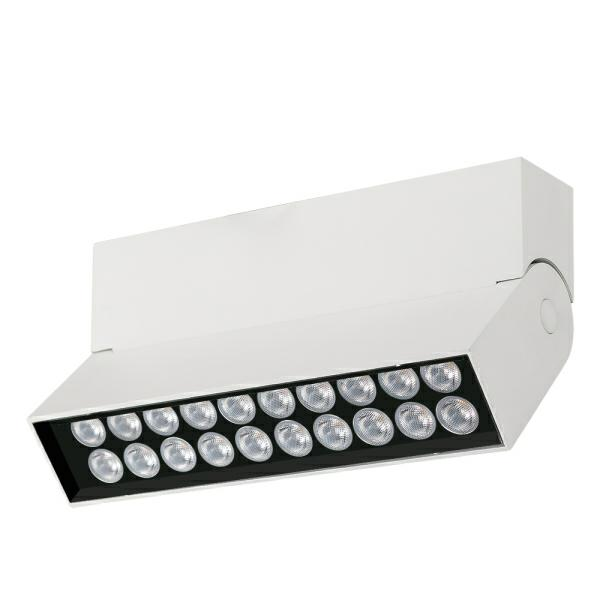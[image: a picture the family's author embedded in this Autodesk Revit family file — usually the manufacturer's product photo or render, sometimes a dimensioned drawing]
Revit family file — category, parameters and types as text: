
# Revit family: LOFT-SURFACE-10W
name_source: partatom
category: Осветительные приборы
revit_build: Autodesk Revit 2017 (Build: 20160225_1515(x64)
units: mm (PartAtom-declared; Revit-internal decimal feet)

## family parameters
Всегда вертикально = Да
Источник света = Да
На основе рабочей плоскости = Нет
Общий = Нет
При загрузке вырезать с полостями = Нет
Размер круглого соединителя = Использовать диаметр
Тип детали = Нормальный
Точка расчета площади = Нет

## types (6) — shared parameters
ADSK_Единица измерения = шт.
ADSK_Завод-изготовитель = ARLIGHT
ADSK_Классификация нагрузок = Освещение
ADSK_Количество фаз = 1
ADSK_Количество фаз числовое = 1
ADSK_Коэффициент мощности = 0.95
ADSK_Масса_Текст = 0.565
ADSK_Наименование = Светильник
ADSK_Напряжение = 230 В
ADSK_Номинальная мощность = 10 Вт
ADSK_Полная мощность = 11 В·А
ADSK_Размер_Высота = 100 мм
ADSK_Размер_Длина = 170 мм
ADSK_Размер_Ширина = 36 мм
ADSK_Ток = 0 А
ARL_Драйвер = Встроенный (DC300mA 25-40V)
ARL_Индекс цветопередачи = >90
ARL_Класс защиты от поражения электрическим током = I
ARL_Класс пылевлагозащиты = IP40
ARL_Область использования = Для освещения в квартирах, офисах, музеях, магазинах с высокими требованиями к качеству света
ARL_Рабочая температура окружающей среды = -20...+40 °C
ARL_Серия = LOFT
ARL_Способ монтажа = Накладной
ARL_Тип товара = Светильник
ARL_Угол обзора = 24°
URL = https://arlight.ru
Видимая форма излучения при визуализации = Нет
Группа модели = Светильники
Изготовитель = ARLIGHT
Изготовитель (сайт) = www.arlight.ru
Изготовитель (телефон) = 8 800 505 26 29
Излучение по длине прямоугольника = 168 мм
Излучение по ширине прямоугольника = 34 мм
Полная установленная мощность = 11 В·А
Разработчик = НТЦ Конструктор
Разработчик (URL) = https://constructor.ru
Разработчик (телефон) = +7 (495) 781-05-35
Светофильтр = 16777215
Смещение цветовой температуры при затухании лампы = <Нет>
Угол наклона = 90.00°

## per-type parameters (varying)
| type | ADSK_Код изделия | ADSK_Марка | ARL_Материал корпуса | ARL_Обозначение корпуса | ARL_Цвет покрытия | ARL_Цвет свечения | Комментарии к типоразмеру | Описание | Файл фотометрической сетки |
| 026212 Светильник SP-LOFT-SURFACE-S170-10W White6000 (WH, 24 deg) | Арт. 026214 | SP-LOFT-SURFACE-S170-10W Warm3000 | Металл, белый | Корпус прямоугольный, алюминий, цвет белый | Белый | Теплый 3000K | Арт. 026214 | Накладной поворотный светильник 10 Вт. Цвет ТЕПЛЫЙ 3000K, св.поток 500-550лм, CRI(Ra)>90, угол 24°. Угол наклона 45°. Корпус прямоугольный, белый алюминий, IP40. Размер LxHxW 170x100x36 мм. Питание AC 220-240V, 10 Вт, драйвер встроенный (DC300mA 25-40V) | 026214_SP-LOFT-SURFACE-S170-10W Warm3000 (WH, 24 deg).ies |
| 026213 Светильник SP-LOFT-SURFACE-S170-10W Day4000 (WH, 24 deg) | Арт. 026213 | SP-LOFT-SURFACE-S170-10W Day4000 | Металл, белый | Корпус прямоугольный, алюминий, цвет белый | Белый | Дневной 4000K | Арт. 026213 | Накладной поворотный светильник 10 Вт. Цвет ДНЕВНОЙ 4000K, св.поток 540-600лм, CRI(Ra)>90, угол 24°. Угол наклона 45°. Корпус прямоугольный, белый алюминий, IP40. Размер LxHxW 170x100x36 мм. Питание AC 220-240V, 10 Вт, драйвер встроенный (DC300mA 25-40V) | 026213_SP-LOFT-SURFACE-S170-10W Day4000 (WH, 24 deg).ies |
| 026214 Светильник SP-LOFT-SURFACE-S170-10W Warm3000 (WH, 24 deg) | Арт. 026214 | SP-LOFT-SURFACE-S170-10W Warm3000 | Металл, белый | Корпус прямоугольный, алюминий, цвет белый | Белый | Теплый 3000K | Арт. 026214 | Накладной поворотный светильник 10 Вт. Цвет ТЕПЛЫЙ 3000K, св.поток 500-550лм, CRI(Ra)>90, угол 24°. Угол наклона 45°. Корпус прямоугольный, белый алюминий, IP40. Размер LxHxW 170x100x36 мм. Питание AC 220-240V, 10 Вт, драйвер встроенный (DC300mA 25-40V) | 026214_SP-LOFT-SURFACE-S170-10W Warm3000 (WH, 24 deg).ies |
| 026211 Светильник SP-LOFT-SURFACE-S170-10W White6000 (BK, 24 deg) | Арт. 026211 | SP-LOFT-SURFACE-S170-10W White6000 | Металл, чёрный | Корпус прямоугольный, алюминий, цвет черный | Черный | Белый 6000K | Арт. 026211 | Накладной поворотный светильник 10 Вт. Цвет БЕЛЫЙ 6000K, св.поток 540-600лм, CRI(Ra)>90, угол 24°. Угол наклона 45°. Корпус прямоугольный, черный алюминий, IP40. Размер LxHxW 170x100x36 мм. Питание AC 220-240V, 10 Вт, драйвер встроенный (DC300mA 25-40V) | 026211_SP-LOFT-SURFACE-S170-10W White6000 (BK, 24 deg).ies |
| 026210 Светильник SP-LOFT-SURFACE-S170-10W Day4000 (BK, 24 deg) | Арт. 026210 | SP-LOFT-SURFACE-S170-10W Day4000 | Металл, чёрный | Корпус прямоугольный, алюминий, цвет черный | Черный | Дневной 4000K | Арт. 026210 | Накладной поворотный светильник 10 Вт. Цвет ДНЕВНОЙ 4000K, св.поток 540-600лм, CRI(Ra)>90, угол 24°. Угол наклона 45°. Корпус прямоугольный, черный алюминий, IP40. Размер LxHxW 170x100x36 мм. Питание AC 220-240V, 10 Вт, драйвер встроенный (DC300mA 25-40V) | 026210_SP-LOFT-SURFACE-S170-10W Day4000 (BK, 24 deg).ies |
| 025656 Светильник SP-LOFT-SURFACE-S170-10W Warm3000 (BK, 24 deg) | Арт. 025656 | SP-LOFT-SURFACE-S170-10W Warm3000 | Металл, чёрный | Корпус прямоугольный, алюминий, цвет черный | Черный | Теплый 3000K | Арт. 025656 | Накладной поворотный светильник 10 Вт. Цвет ТЕПЛЫЙ 3000K, св.поток 500-550лм, CRI(Ra)>90, угол 24°. Угол наклона 45°. Корпус прямоугольный, черный алюминий, IP40. Размер LxHxW 170x100x36 мм. Питание AC 220-240V, 10 Вт, драйвер встроенный (DC300mA 25-40V) | 025656_SP-LOFT-SURFACE-S170-10W Warm3000 (BK, 24 deg).ies |
